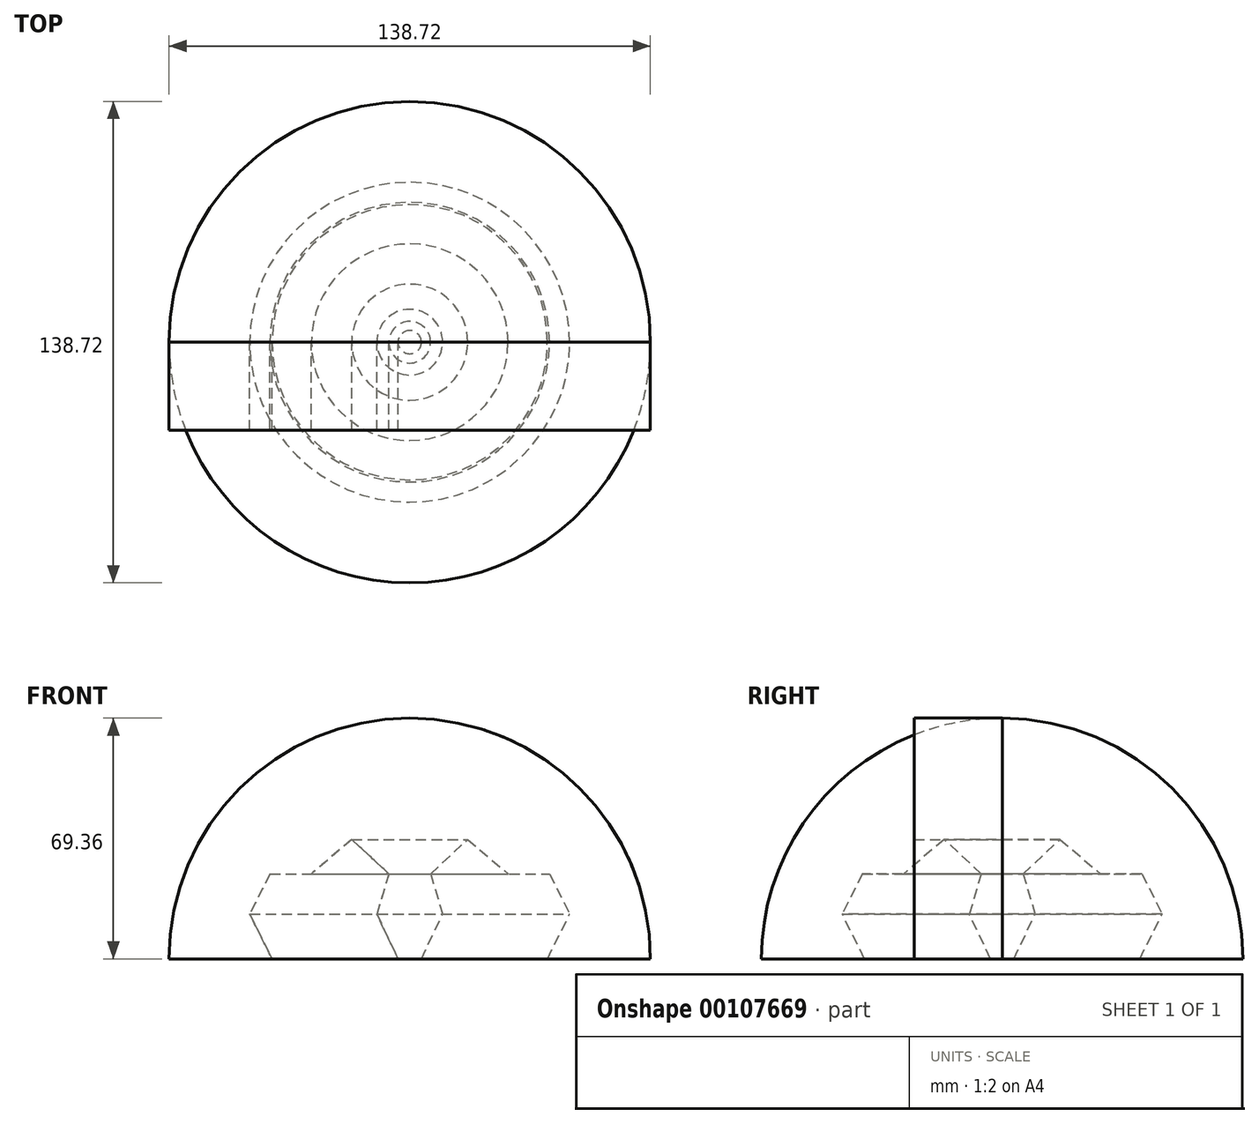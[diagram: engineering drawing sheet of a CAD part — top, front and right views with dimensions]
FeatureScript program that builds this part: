
annotation { "Feature Type Name" : "Feature", "Feature Type Description" : "" }
export const myFeature = defineFeature(function(context is Context, id is Id, definition is map)
    precondition{}
    {
        {
            var Q0;
            Q0=qCreatedBy(makeId("Front.planeOp"),FACE);
            var sketch = newSketch(context, id + "F0", { "sketchPlane" : qUnion([Q0])});
            skArc(sketch, "E0", {"start": v(69.36, 0) * mm, "mid": v(0, 69.36) * mm, "end": v(-69.36, 0) * mm});
            skLineSegment(sketch, "E1", {"start": v(-69.36, 0) * mm, "end": v(69.36, 0) * mm});
            skLineSegment(sketch, "E2", {"start": v(0, 0) * mm, "end": v(0, 69.36) * mm});
            skLineSegment(sketch, "E3", {"start": v(-23, 12.88) * mm, "end": v(-16.7, 0) * mm});
            skLineSegment(sketch, "E4", {"start": v(-23, 12.88) * mm, "end": v(-9.48, 12.88) * mm});
            skLineSegment(sketch, "E5", {"start": v(-9.48, 12.88) * mm, "end": v(-16.7, 0) * mm});
            skLineSegment(sketch, "E6", {"start": v(-9.48, 12.88) * mm, "end": v(-3.35, 0) * mm});
            skLineSegment(sketch, "E7", {"start": v(-23, 12.88) * mm, "end": v(-28.65, 0) * mm});
            skLineSegment(sketch, "E8", {"start": v(-23, 12.88) * mm, "end": v(-16.7, 24.5) * mm});
            skLineSegment(sketch, "E9", {"start": v(-16.7, 24.5) * mm, "end": v(-9.48, 12.88) * mm});
            skLineSegment(sketch, "E10", {"start": v(-16.7, 24.5) * mm, "end": v(-28.34, 24.5) * mm});
            skLineSegment(sketch, "E11", {"start": v(-16.7, 24.5) * mm, "end": v(-16.7, 34.41) * mm});
            skLineSegment(sketch, "E12", {"start": v(-16.7, 24.5) * mm, "end": v(-6.02, 24.5) * mm});
            skLineSegment(sketch, "E13", {"start": v(-28.34, 24.5) * mm, "end": v(-23, 12.88) * mm});
            skLineSegment(sketch, "E14", {"start": v(-6.02, 24.5) * mm, "end": v(-9.48, 12.88) * mm});
            skLineSegment(sketch, "E15", {"start": v(-16.7, 34.41) * mm, "end": v(-28.34, 24.5) * mm});
            skLineSegment(sketch, "E16", {"start": v(-16.7, 34.41) * mm, "end": v(-6.02, 24.5) * mm});
            skLineSegment(sketch, "E17", {"start": v(-23, 12.88) * mm, "end": v(-34.16, 12.88) * mm});
            skLineSegment(sketch, "E18", {"start": v(-28.65, 0) * mm, "end": v(-34.16, 12.88) * mm});
            skLineSegment(sketch, "E19", {"start": v(-28.65, 0) * mm, "end": v(-39.66, 0) * mm});
            skLineSegment(sketch, "E20", {"start": v(-39.66, 0) * mm, "end": v(-34.16, 12.88) * mm});
            skLineSegment(sketch, "E21", {"start": v(-46.1, 12.88) * mm, "end": v(-39.66, 0) * mm});
            skLineSegment(sketch, "E22", {"start": v(-46.1, 12.88) * mm, "end": v(-34.16, 12.88) * mm});
            skLineSegment(sketch, "E23", {"start": v(-34.16, 12.88) * mm, "end": v(-40.29, 24.5) * mm});
            skLineSegment(sketch, "E24", {"start": v(-40.29, 24.5) * mm, "end": v(-28.34, 24.5) * mm});
            skLineSegment(sketch, "E25", {"start": v(-34.16, 12.88) * mm, "end": v(-28.34, 24.5) * mm});
            skLineSegment(sketch, "E26", {"start": v(-40.29, 24.5) * mm, "end": v(-46.1, 12.88) * mm});
            skSolve(sketch);
        }
        {
            var Q0;
            {var subQ3=sQuery(id+"F0.wireOp",EDGE,"E2");Q0=makeQuery(id+"F0.imprint","IMPRINT",FACE,{"disambiguationData":[TD([[makeQuery(id+"F0.imprint","IMPRINT",EDGE,{"derivedFrom":subQ3}),1.0]])]});}
            var Q1;
            Q1=sQuery(id+"F0.wireOp",EDGE,"E2");
            revolve(context, id + "F1", {"entities" : qUnion([Q0]), "axis" : qUnion([Q1]), "revolveType" : RevolveType.FULL});
        }
        {
            var Q0;
            {var subQ5=sQuery(id+"F0.wireOp",EDGE,"E2");Q0=makeQuery(id+"F0.imprint","IMPRINT",FACE,{"disambiguationData":[TD([[makeQuery(id+"F0.imprint","IMPRINT",EDGE,{"derivedFrom":subQ5}),1.0]])]});}
            var Q1;
            {var subQ3=sQuery(id+"F0.wireOp",EDGE,"E2");Q1=makeQuery(id+"F0.imprint","IMPRINT",FACE,{"disambiguationData":[TD([[makeQuery(id+"F0.imprint","IMPRINT",EDGE,{"derivedFrom":subQ3}),-1.0]])]});}
            extrude(context, id + "F2", {"entities" : qUnion([Q0, Q1]), "depth" : 25.4 * mm});
        }
    });
